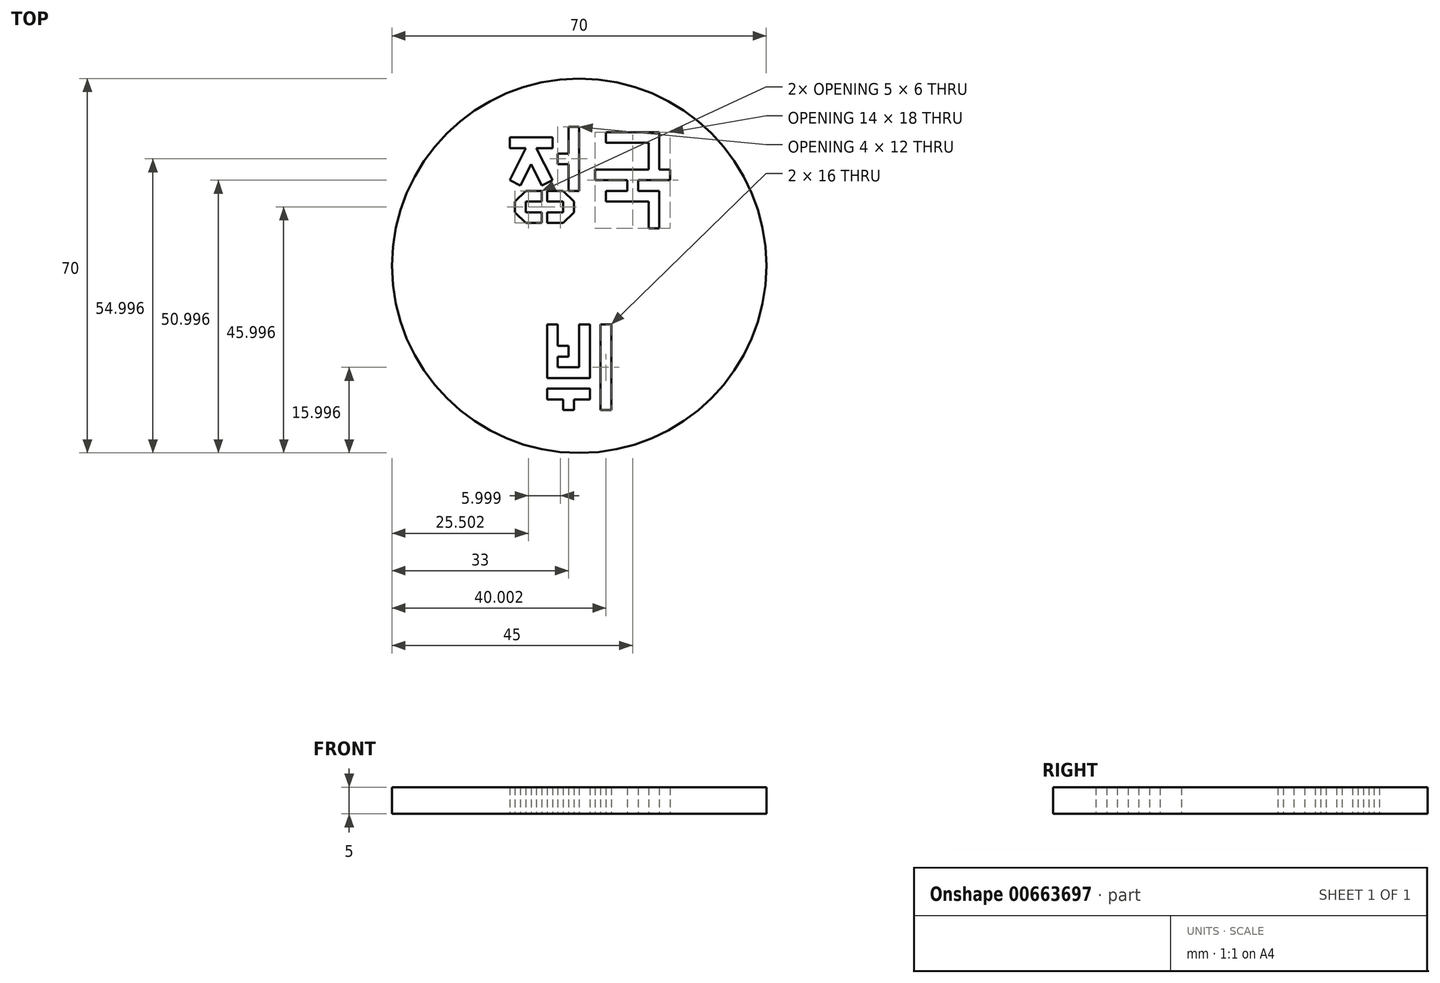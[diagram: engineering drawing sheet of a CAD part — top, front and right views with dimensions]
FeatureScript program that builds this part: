
annotation { "Feature Type Name" : "Feature", "Feature Type Description" : "" }
export const myFeature = defineFeature(function(context is Context, id is Id, definition is map)
    precondition{}
    {
        {
            var Q0;
            Q0=qCreatedBy(makeId("Top.planeOp"),FACE);
            var sketch = newSketch(context, id + "F0", { "sketchPlane" : qUnion([Q0])});
            skLineSegment(sketch, "E0.bottom", {"start": v(-56.96, 29.95) * mm, "end": v(-48.96, 29.95) * mm});
            skLineSegment(sketch, "E0.left", {"start": v(-56.96, 29.95) * mm, "end": v(-56.96, 27.95) * mm});
            skLineSegment(sketch, "E0.right", {"start": v(-48.96, 29.95) * mm, "end": v(-48.96, 27.95) * mm});
            skLineSegment(sketch, "E1", {"start": v(-51.96, 27.95) * mm, "end": v(-48.96, 21.95) * mm});
            skLineSegment(sketch, "E2", {"start": v(-48.96, 21.95) * mm, "end": v(-50.96, 20.95) * mm});
            skLineSegment(sketch, "E3", {"start": v(-52.96, 24.95) * mm, "end": v(-50.96, 20.95) * mm});
            skLineSegment(sketch, "E4", {"start": v(-52.96, 24.95) * mm, "end": v(-54.96, 20.95) * mm});
            skLineSegment(sketch, "E5", {"start": v(-53.96, 27.95) * mm, "end": v(-56.96, 21.95) * mm});
            skLineSegment(sketch, "E6", {"start": v(-56.96, 21.95) * mm, "end": v(-54.96, 20.95) * mm});
            skLineSegment(sketch, "E7", {"start": v(-45.96, 19.95) * mm, "end": v(-45.96, 24.95) * mm});
            skLineSegment(sketch, "E8", {"start": v(-45.96, 24.95) * mm, "end": v(-47.96, 24.95) * mm});
            skLineSegment(sketch, "E9", {"start": v(-47.96, 24.95) * mm, "end": v(-47.96, 26.95) * mm});
            skLineSegment(sketch, "E10", {"start": v(-47.96, 26.95) * mm, "end": v(-45.96, 26.95) * mm});
            skLineSegment(sketch, "E11", {"start": v(-45.96, 26.95) * mm, "end": v(-45.96, 31.95) * mm});
            skLineSegment(sketch, "E12", {"start": v(-55.96, 17.95) * mm, "end": v(-55.96, 15.95) * mm});
            skLineSegment(sketch, "E13", {"start": v(-53.96, 13.95) * mm, "end": v(-55.96, 15.95) * mm});
            skLineSegment(sketch, "E14", {"start": v(-55.96, 17.95) * mm, "end": v(-53.96, 19.95) * mm});
            skLineSegment(sketch, "E15.bottom", {"start": v(-38.96, 30.95) * mm, "end": v(-28.96, 30.95) * mm});
            skLineSegment(sketch, "E15.top", {"start": v(-38.96, 28.95) * mm, "end": v(-30.96, 28.95) * mm});
            skLineSegment(sketch, "E15.left", {"start": v(-38.96, 30.95) * mm, "end": v(-38.96, 28.95) * mm});
            skLineSegment(sketch, "E15.right", {"start": v(-28.96, 30.95) * mm, "end": v(-28.96, 28.95) * mm});
            skLineSegment(sketch, "E16.left", {"start": v(-28.96, 28.95) * mm, "end": v(-28.96, 23.95) * mm});
            skLineSegment(sketch, "E16.right", {"start": v(-30.96, 28.95) * mm, "end": v(-30.96, 23.95) * mm});
            skLineSegment(sketch, "E17", {"start": v(-28.96, 23.95) * mm, "end": v(-26.96, 23.95) * mm});
            skLineSegment(sketch, "E18", {"start": v(-26.96, 23.95) * mm, "end": v(-26.96, 21.95) * mm});
            skLineSegment(sketch, "E19", {"start": v(-26.96, 21.95) * mm, "end": v(-32.96, 21.95) * mm});
            skLineSegment(sketch, "E20", {"start": v(-32.96, 21.95) * mm, "end": v(-32.96, 19.95) * mm});
            skLineSegment(sketch, "E21", {"start": v(-32.96, 19.95) * mm, "end": v(-28.96, 19.95) * mm});
            skLineSegment(sketch, "E22", {"start": v(-28.96, 19.95) * mm, "end": v(-28.96, 12.95) * mm});
            skLineSegment(sketch, "E23", {"start": v(-28.96, 12.95) * mm, "end": v(-30.96, 12.95) * mm});
            skLineSegment(sketch, "E24", {"start": v(-30.96, 12.95) * mm, "end": v(-30.96, 17.95) * mm});
            skLineSegment(sketch, "E25", {"start": v(-30.96, 17.95) * mm, "end": v(-38.96, 17.95) * mm});
            skLineSegment(sketch, "E26", {"start": v(-38.96, 17.95) * mm, "end": v(-38.96, 19.95) * mm});
            skLineSegment(sketch, "E27", {"start": v(-38.96, 19.95) * mm, "end": v(-34.96, 19.95) * mm});
            skLineSegment(sketch, "E28", {"start": v(-34.96, 19.95) * mm, "end": v(-34.96, 21.95) * mm});
            skLineSegment(sketch, "E29", {"start": v(-34.96, 21.95) * mm, "end": v(-40.96, 21.95) * mm});
            skLineSegment(sketch, "E30", {"start": v(-40.96, 21.95) * mm, "end": v(-40.96, 23.95) * mm});
            skLineSegment(sketch, "E31", {"start": v(-40.96, 23.95) * mm, "end": v(-30.96, 23.95) * mm});
            skLineSegment(sketch, "E32", {"start": v(-49.96, -5.05) * mm, "end": v(-49.96, -15.05) * mm});
            skLineSegment(sketch, "E33", {"start": v(-49.96, -15.05) * mm, "end": v(-41.96, -15.05) * mm});
            skLineSegment(sketch, "E34", {"start": v(-41.96, -15.05) * mm, "end": v(-41.96, -5.05) * mm});
            skLineSegment(sketch, "E35", {"start": v(-41.96, -5.05) * mm, "end": v(-43.96, -5.05) * mm});
            skLineSegment(sketch, "E36", {"start": v(-43.96, -5.05) * mm, "end": v(-43.96, -13.05) * mm});
            skLineSegment(sketch, "E37", {"start": v(-43.96, -13.05) * mm, "end": v(-47.96, -13.05) * mm});
            skLineSegment(sketch, "E38", {"start": v(-47.96, -13.05) * mm, "end": v(-47.96, -11.05) * mm});
            skLineSegment(sketch, "E39", {"start": v(-47.96, -11.05) * mm, "end": v(-45.96, -11.05) * mm});
            skLineSegment(sketch, "E40", {"start": v(-45.96, -11.05) * mm, "end": v(-45.96, -9.05) * mm});
            skLineSegment(sketch, "E41", {"start": v(-45.96, -9.05) * mm, "end": v(-47.96, -9.05) * mm});
            skLineSegment(sketch, "E42", {"start": v(-47.96, -9.05) * mm, "end": v(-47.96, -5.05) * mm});
            skLineSegment(sketch, "E43", {"start": v(-49.96, -17.05) * mm, "end": v(-41.96, -17.05) * mm});
            skLineSegment(sketch, "E44", {"start": v(-41.96, -17.05) * mm, "end": v(-41.96, -19.05) * mm});
            skLineSegment(sketch, "E45", {"start": v(-41.96, -19.05) * mm, "end": v(-44.96, -19.05) * mm});
            skLineSegment(sketch, "E46", {"start": v(-44.96, -19.05) * mm, "end": v(-44.96, -21.05) * mm});
            skLineSegment(sketch, "E47", {"start": v(-44.96, -21.05) * mm, "end": v(-46.96, -21.05) * mm});
            skLineSegment(sketch, "E48", {"start": v(-46.96, -21.05) * mm, "end": v(-46.96, -19.05) * mm});
            skLineSegment(sketch, "E49", {"start": v(-46.96, -19.05) * mm, "end": v(-49.96, -19.05) * mm});
            skLineSegment(sketch, "E50", {"start": v(-49.96, -19.05) * mm, "end": v(-49.96, -17.05) * mm});
            skLineSegment(sketch, "E51", {"start": v(-47.96, -5.05) * mm, "end": v(-49.96, -5.05) * mm});
            skLineSegment(sketch, "E52", {"start": v(-39.96, -5.05) * mm, "end": v(-37.96, -5.05) * mm});
            skLineSegment(sketch, "E53", {"start": v(-37.96, -5.05) * mm, "end": v(-37.96, -21.05) * mm});
            skLineSegment(sketch, "E54", {"start": v(-37.96, -21.05) * mm, "end": v(-39.96, -21.05) * mm});
            skLineSegment(sketch, "E55", {"start": v(-39.96, -21.05) * mm, "end": v(-39.96, -5.05) * mm});
            skCircle(sketch, "E56", {"center": v(-43.96, 5.95) * mm, "radius": 35 * mm});
            skLineSegment(sketch, "E57", {"start": v(-56.96, 27.95) * mm, "end": v(-53.96, 27.95) * mm});
            skLineSegment(sketch, "E58", {"start": v(-51.96, 27.95) * mm, "end": v(-48.96, 27.95) * mm});
            skLineSegment(sketch, "E59", {"start": v(-53.96, 19.95) * mm, "end": v(-50.96, 19.95) * mm});
            skLineSegment(sketch, "E60", {"start": v(-50.96, 19.95) * mm, "end": v(-50.96, 17.95) * mm});
            skLineSegment(sketch, "E61", {"start": v(-50.96, 17.95) * mm, "end": v(-53.96, 17.95) * mm});
            skLineSegment(sketch, "E62", {"start": v(-53.96, 17.95) * mm, "end": v(-53.96, 15.95) * mm});
            skLineSegment(sketch, "E63", {"start": v(-53.96, 15.95) * mm, "end": v(-50.96, 15.95) * mm});
            skLineSegment(sketch, "E64", {"start": v(-50.96, 15.95) * mm, "end": v(-50.96, 13.95) * mm});
            skLineSegment(sketch, "E65", {"start": v(-50.96, 13.95) * mm, "end": v(-53.96, 13.95) * mm});
            skLineSegment(sketch, "E66", {"start": v(-45.96, 19.95) * mm, "end": v(-43.96, 19.95) * mm});
            skLineSegment(sketch, "E67", {"start": v(-43.96, 19.95) * mm, "end": v(-43.96, 31.95) * mm});
            skLineSegment(sketch, "E68", {"start": v(-43.96, 31.95) * mm, "end": v(-45.96, 31.95) * mm});
            skLineSegment(sketch, "E69", {"start": v(-49.96, 19.95) * mm, "end": v(-49.96, 17.95) * mm});
            skLineSegment(sketch, "E70", {"start": v(-49.96, 17.95) * mm, "end": v(-46.96, 17.95) * mm});
            skLineSegment(sketch, "E71", {"start": v(-46.96, 17.95) * mm, "end": v(-46.96, 15.95) * mm});
            skLineSegment(sketch, "E72", {"start": v(-46.96, 15.95) * mm, "end": v(-49.96, 15.95) * mm});
            skLineSegment(sketch, "E73", {"start": v(-49.96, 15.95) * mm, "end": v(-49.96, 13.95) * mm});
            skLineSegment(sketch, "E74", {"start": v(-49.96, 13.95) * mm, "end": v(-46.96, 13.95) * mm});
            skLineSegment(sketch, "E75", {"start": v(-44.96, 15.95) * mm, "end": v(-46.96, 13.95) * mm});
            skLineSegment(sketch, "E76", {"start": v(-49.96, 19.95) * mm, "end": v(-46.96, 19.95) * mm});
            skLineSegment(sketch, "E77", {"start": v(-44.96, 15.95) * mm, "end": v(-44.96, 17.95) * mm});
            skLineSegment(sketch, "E78", {"start": v(-46.96, 19.95) * mm, "end": v(-44.96, 17.95) * mm});
            skSolve(sketch);
        }
        {
            var Q0;
            Q0=makeQuery(id+"F0.imprint","IMPRINT",FACE,{"disambiguationData":[TD([[makeQuery(id+"F0.imprint","IMPRINT",EDGE,{"derivedFrom":sQuery(id+"F0.wireOp",EDGE,"E0.bottom")}),1.0]])]});
            extrude(context, id + "F1", {"entities" : qUnion([Q0]), "depth" : 5 * mm, "offsetDistance" : 25 * mm});
        }
    });
